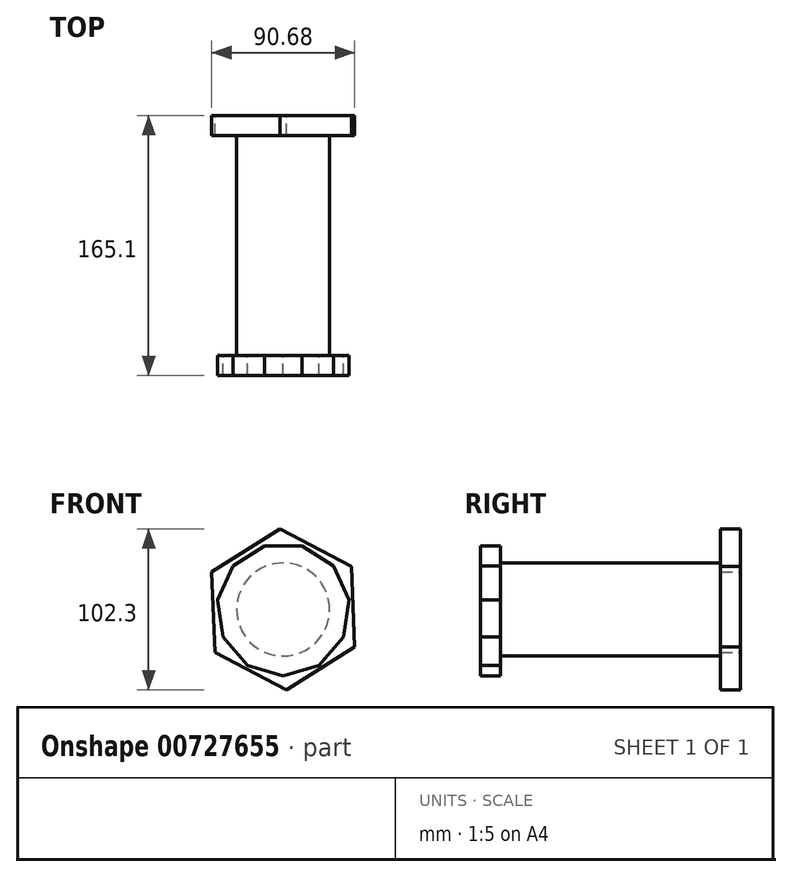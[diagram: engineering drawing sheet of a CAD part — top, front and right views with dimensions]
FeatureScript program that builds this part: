
annotation { "Feature Type Name" : "Feature", "Feature Type Description" : "" }
export const myFeature = defineFeature(function(context is Context, id is Id, definition is map)
    precondition{}
    {
        {
            var Q0;
            Q0=qCreatedBy(makeId("Front.planeOp"),FACE);
            var sketch = newSketch(context, id + "F0", { "sketchPlane" : qUnion([Q0])});
            skCircle(sketch, "E0.cCircle", {"center": v(0, 0) * mm, "radius": 40.42 * mm, "construction": true});
            skLineSegment(sketch, "E0.0", {"start": v(-11.87, 40.42) * mm, "end": v(11.87, 40.42) * mm});
            skLineSegment(sketch, "E0.1", {"start": v(11.87, 40.42) * mm, "end": v(31.84, 27.6) * mm});
            skLineSegment(sketch, "E0.2", {"start": v(31.84, 27.6) * mm, "end": v(41.7, 6) * mm});
            skLineSegment(sketch, "E0.3", {"start": v(41.7, 6) * mm, "end": v(38.32, -17.5) * mm});
            skLineSegment(sketch, "E0.4", {"start": v(38.32, -17.5) * mm, "end": v(22.78, -35.44) * mm});
            skLineSegment(sketch, "E0.5", {"start": v(22.78, -35.44) * mm, "end": v(0, -42.13) * mm});
            skLineSegment(sketch, "E0.6", {"start": v(0, -42.13) * mm, "end": v(-22.78, -35.44) * mm});
            skLineSegment(sketch, "E0.7", {"start": v(-22.78, -35.44) * mm, "end": v(-38.32, -17.5) * mm});
            skLineSegment(sketch, "E0.8", {"start": v(-38.32, -17.5) * mm, "end": v(-41.7, 6) * mm});
            skLineSegment(sketch, "E0.9", {"start": v(-41.7, 6) * mm, "end": v(-31.84, 27.6) * mm});
            skLineSegment(sketch, "E0.10", {"start": v(-31.84, 27.6) * mm, "end": v(-11.87, 40.42) * mm});
            skPoint(sketch, "E0.0.midPoint", {"position": v(0, 40.42) * mm});
            skSolve(sketch);
        }
        {
            var Q0;
            Q0=makeQuery(id+"F0.imprint","IMPRINT",FACE,{"disambiguationData":[TD([[makeQuery(id+"F0.imprint","IMPRINT",EDGE,{"derivedFrom":sQuery(id+"F0.wireOp",EDGE,"E0.0")}),-1.0]])]});
            extrude(context, id + "F1", {"entities" : qUnion([Q0]), "depth" : 12.7 * mm, "offsetDistance" : 25.4 * mm});
        }
        {
            var Q0;
            Q0=makeQuery(id+"F1.opExtrude","CAP_FACE",FACE,{"disambiguationData":[OSD([sQuery(id+"F0.wireOp",EDGE,"E0.0"),sQuery(id+"F0.wireOp",EDGE,"E0.1"),sQuery(id+"F0.wireOp",EDGE,"E0.2"),sQuery(id+"F0.wireOp",EDGE,"E0.3"),sQuery(id+"F0.wireOp",EDGE,"E0.4"),sQuery(id+"F0.wireOp",EDGE,"E0.5"),sQuery(id+"F0.wireOp",EDGE,"E0.6"),sQuery(id+"F0.wireOp",EDGE,"E0.7"),sQuery(id+"F0.wireOp",EDGE,"E0.8"),sQuery(id+"F0.wireOp",EDGE,"E0.9"),sQuery(id+"F0.wireOp",EDGE,"E0.10")])],"isStart":true});
            var sketch = newSketch(context, id + "F2", { "sketchPlane" : qUnion([Q0])});
            skCircle(sketch, "E1", {"center": v(0, 0) * mm, "radius": 29.53 * mm});
            skSolve(sketch);
        }
        {
            var Q0;
            Q0=makeQuery(id+"F2.imprint","IMPRINT",FACE,{"disambiguationData":[TD([[makeQuery(id+"F2.imprint","IMPRINT",EDGE,{"derivedFrom":sQuery(id+"F2.wireOp",EDGE,"E1")}),1.0]])]});
            extrude(context, id + "F3", {"entities" : qUnion([Q0]), "operationType" : NewBodyOperationType.ADD, "depth" : 152.4 * mm, "offsetDistance" : 25.4 * mm});
        }
        {
            var Q0;
            Q0=makeQuery(id+"F3.opExtrude","CAP_FACE",FACE,{"disambiguationData":[OSD([sQuery(id+"F2.wireOp",EDGE,"E1")])],"isStart":false});
            var sketch = newSketch(context, id + "F4", { "sketchPlane" : qUnion([Q0])});
            skCircle(sketch, "E2.cCircle", {"center": v(0, 0) * mm, "radius": 44.34 * mm, "construction": true});
            skLineSegment(sketch, "E2.0", {"start": v(2.07, 51.15) * mm, "end": v(45.34, 23.78) * mm});
            skLineSegment(sketch, "E2.1", {"start": v(45.34, 23.78) * mm, "end": v(43.27, -27.37) * mm});
            skLineSegment(sketch, "E2.2", {"start": v(43.27, -27.37) * mm, "end": v(-2.07, -51.15) * mm});
            skLineSegment(sketch, "E2.3", {"start": v(-2.07, -51.15) * mm, "end": v(-45.34, -23.78) * mm});
            skLineSegment(sketch, "E2.4", {"start": v(-45.34, -23.78) * mm, "end": v(-43.27, 27.37) * mm});
            skLineSegment(sketch, "E2.5", {"start": v(-43.27, 27.37) * mm, "end": v(2.07, 51.15) * mm});
            skPoint(sketch, "E2.0.midPoint", {"position": v(23.7, 37.47) * mm});
            skSolve(sketch);
        }
        {
            var Q0;
            Q0=makeQuery(id+"F4.imprint","IMPRINT",FACE,{"disambiguationData":[TD([[makeQuery(id+"F4.imprint","IMPRINT",EDGE,{"derivedFrom":sQuery(id+"F4.wireOp",EDGE,"E2.0")}),-1.0]])]});
            extrude(context, id + "F5", {"entities" : qUnion([Q0]), "operationType" : NewBodyOperationType.ADD, "oppositeDirection" : true, "depth" : 12.7 * mm, "offsetDistance" : 25.4 * mm});
        }
    });
